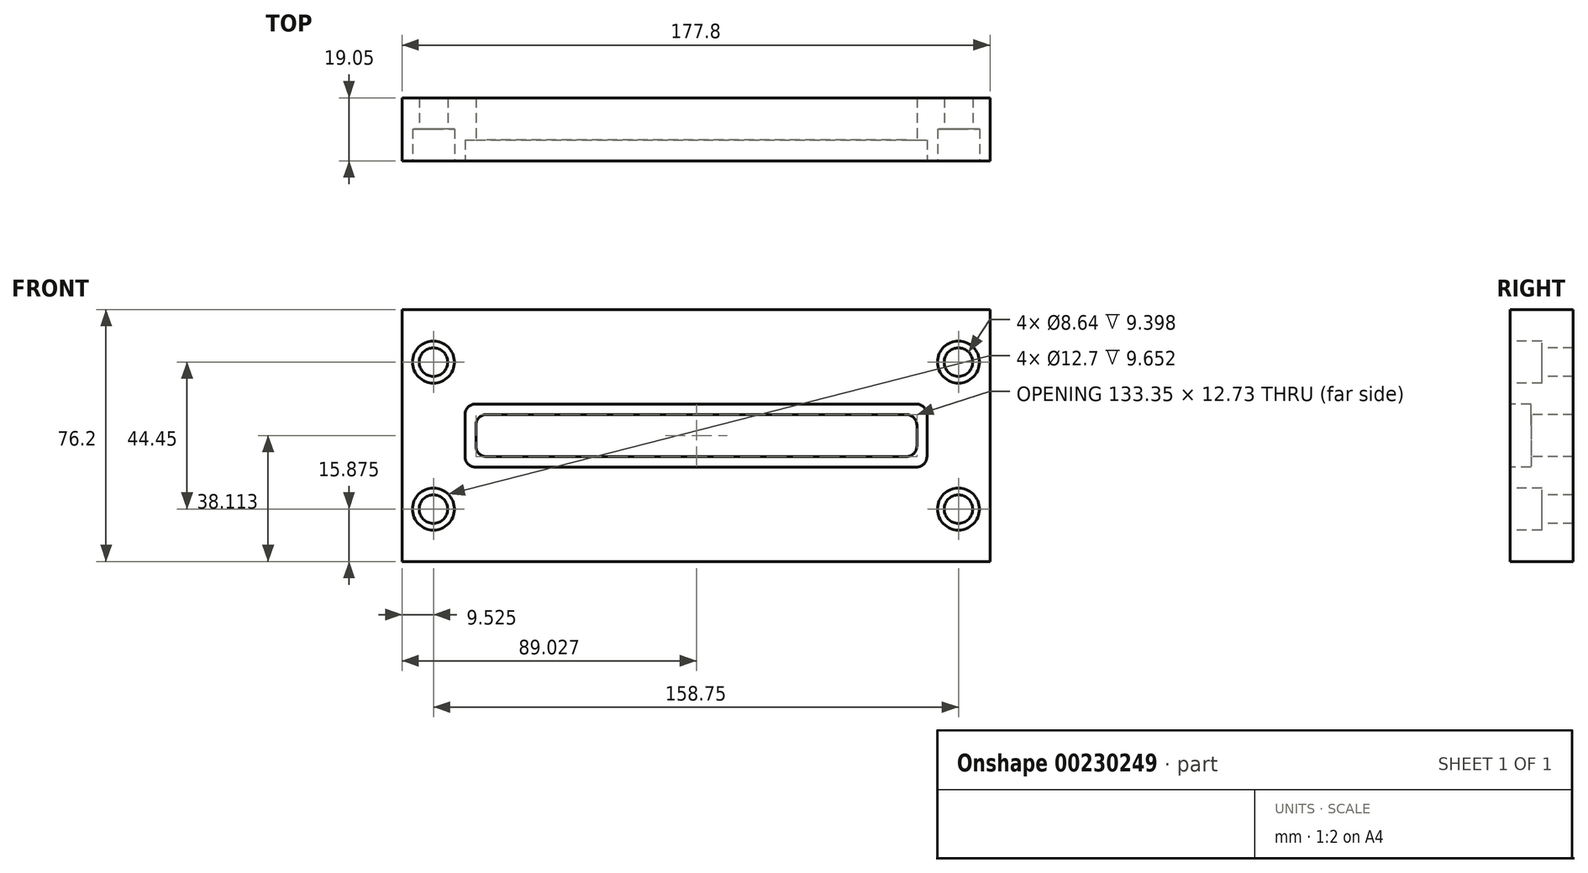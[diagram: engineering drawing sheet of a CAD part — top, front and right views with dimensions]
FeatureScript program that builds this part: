
annotation { "Feature Type Name" : "Feature", "Feature Type Description" : "" }
export const myFeature = defineFeature(function(context is Context, id is Id, definition is map)
    precondition{}
    {
        {
            var Q0;
            Q0=qCreatedBy(makeId("Front.planeOp"),FACE);
            var sketch = newSketch(context, id + "F0", { "sketchPlane" : qUnion([Q0])});
            skLineSegment(sketch, "E0.bottom", {"start": v(0, 0) * mm, "end": v(177.8, 0) * mm});
            skLineSegment(sketch, "E0.top", {"start": v(0, 76.2) * mm, "end": v(177.8, 76.2) * mm});
            skLineSegment(sketch, "E0.left", {"start": v(0, 0) * mm, "end": v(0, 76.2) * mm});
            skLineSegment(sketch, "E0.right", {"start": v(177.8, 0) * mm, "end": v(177.8, 76.2) * mm});
            skSolve(sketch);
        }
        {
            var Q0;
            Q0 = qSketchRegion(id + "F0", true);
            extrude(context, id + "F1", {"entities" : qUnion([Q0]), "depth" : 19.05 * mm});
        }
        {
            var Q0;
            Q0=makeQuery(id+"F1.opExtrude","CAP_FACE",FACE,{"disambiguationData":[OSD([sQuery(id+"F0.wireOp",EDGE,"E0.bottom"),sQuery(id+"F0.wireOp",EDGE,"E0.top"),sQuery(id+"F0.wireOp",EDGE,"E0.left"),sQuery(id+"F0.wireOp",EDGE,"E0.right")])],"isStart":false});
            var sketch = newSketch(context, id + "F2", { "sketchPlane" : qUnion([Q0])});
            skLineSegment(sketch, "E1.bottom", {"start": v(25.53, 31.75) * mm, "end": v(152.53, 31.75) * mm});
            skLineSegment(sketch, "E1.top", {"start": v(25.53, 44.48) * mm, "end": v(152.53, 44.48) * mm});
            skLineSegment(sketch, "E1.left", {"start": v(22.35, 34.92) * mm, "end": v(22.35, 41.3) * mm});
            skLineSegment(sketch, "E1.right", {"start": v(155.7, 34.92) * mm, "end": v(155.7, 41.3) * mm});
            skPoint(sketch, "E2.visualSharp", {"position": v(22.35, 44.48) * mm});
            skArc(sketch, "E2.filletArc", {"start": v(25.53, 44.48) * mm, "mid": v(23.28, 43.55) * mm, "end": v(22.35, 41.3) * mm});
            skPoint(sketch, "E3.visualSharp", {"position": v(22.35, 31.75) * mm});
            skArc(sketch, "E3.filletArc", {"start": v(22.35, 34.92) * mm, "mid": v(23.28, 32.68) * mm, "end": v(25.53, 31.75) * mm});
            skPoint(sketch, "E4.visualSharp", {"position": v(155.7, 31.75) * mm});
            skArc(sketch, "E4.filletArc", {"start": v(152.53, 31.75) * mm, "mid": v(154.77, 32.68) * mm, "end": v(155.7, 34.92) * mm});
            skPoint(sketch, "E5.visualSharp", {"position": v(155.7, 44.48) * mm});
            skArc(sketch, "E5.filletArc", {"start": v(155.7, 41.3) * mm, "mid": v(154.77, 43.55) * mm, "end": v(152.53, 44.48) * mm});
            skSolve(sketch);
        }
        {
            var Q0;
            Q0 = qSketchRegion(id + "F2", true);
            extrude(context, id + "F3", {"entities" : qUnion([Q0]), "operationType" : NewBodyOperationType.REMOVE, "oppositeDirection" : true, "depth" : 25.4 * mm});
        }
        {
            var Q0;
            Q0=makeQuery(id+"F1.opExtrude","CAP_FACE",FACE,{"disambiguationData":[OSD([sQuery(id+"F0.wireOp",EDGE,"E0.bottom"),sQuery(id+"F0.wireOp",EDGE,"E0.top"),sQuery(id+"F0.wireOp",EDGE,"E0.left"),sQuery(id+"F0.wireOp",EDGE,"E0.right")])],"isStart":false});
            var sketch = newSketch(context, id + "F4", { "sketchPlane" : qUnion([Q0])});
            skLineSegment(sketch, "E6.bottom", {"start": v(22.22, 47.65) * mm, "end": v(155.58, 47.65) * mm});
            skLineSegment(sketch, "E6.top", {"start": v(22.22, 28.57) * mm, "end": v(155.58, 28.58) * mm});
            skLineSegment(sketch, "E6.left", {"start": v(19.05, 44.48) * mm, "end": v(19.05, 31.75) * mm});
            skLineSegment(sketch, "E6.right", {"start": v(158.75, 44.48) * mm, "end": v(158.75, 31.75) * mm});
            skPoint(sketch, "E7.visualSharp", {"position": v(19.05, 47.65) * mm});
            skArc(sketch, "E7.filletArc", {"start": v(22.22, 47.65) * mm, "mid": v(19.98, 46.72) * mm, "end": v(19.05, 44.48) * mm});
            skPoint(sketch, "E8.visualSharp", {"position": v(19.05, 28.57) * mm});
            skArc(sketch, "E8.filletArc", {"start": v(19.05, 31.75) * mm, "mid": v(19.98, 29.5) * mm, "end": v(22.22, 28.57) * mm});
            skPoint(sketch, "E9.visualSharp", {"position": v(158.75, 28.58) * mm});
            skArc(sketch, "E9.filletArc", {"start": v(155.58, 28.58) * mm, "mid": v(157.82, 29.5) * mm, "end": v(158.75, 31.75) * mm});
            skPoint(sketch, "E10.visualSharp", {"position": v(158.75, 47.65) * mm});
            skArc(sketch, "E10.filletArc", {"start": v(158.75, 44.48) * mm, "mid": v(157.82, 46.72) * mm, "end": v(155.58, 47.65) * mm});
            skSolve(sketch);
        }
        {
            var Q0;
            Q0 = qSketchRegion(id + "F4", true);
            extrude(context, id + "F5", {"entities" : qUnion([Q0]), "operationType" : NewBodyOperationType.REMOVE, "oppositeDirection" : true, "depth" : 6.35 * mm});
        }
        {
            var Q0;
            Q0=makeQuery(id+"F1.opExtrude","CAP_FACE",FACE,{"disambiguationData":[OSD([sQuery(id+"F0.wireOp",EDGE,"E0.bottom"),sQuery(id+"F0.wireOp",EDGE,"E0.top"),sQuery(id+"F0.wireOp",EDGE,"E0.left"),sQuery(id+"F0.wireOp",EDGE,"E0.right")])],"isStart":false});
            var sketch = newSketch(context, id + "F6", { "sketchPlane" : qUnion([Q0])});
            skLineSegment(sketch, "E11.bottom", {"start": v(9.52, 60.33) * mm, "end": v(168.28, 60.33) * mm});
            skLineSegment(sketch, "E11.top", {"start": v(9.53, 15.87) * mm, "end": v(168.28, 15.88) * mm});
            skLineSegment(sketch, "E11.left", {"start": v(9.52, 60.32) * mm, "end": v(9.53, 15.87) * mm});
            skLineSegment(sketch, "E11.right", {"start": v(168.28, 60.33) * mm, "end": v(168.28, 15.88) * mm});
            skPoint(sketch, "E12", {"position": v(9.52, 60.33) * mm});
            skPoint(sketch, "E13", {"position": v(9.53, 15.87) * mm});
            skPoint(sketch, "E14", {"position": v(168.28, 15.88) * mm});
            skPoint(sketch, "E15", {"position": v(168.28, 60.33) * mm});
            skSolve(sketch);
        }
        {
            var Q0;
            Q0=sQuery(id+"F6.wireOp",VERTEX,"E13");
            var Q1;
            Q1=sQuery(id+"F6.wireOp",VERTEX,"E12");
            var Q2;
            Q2=sQuery(id+"F6.wireOp",VERTEX,"E15");
            var Q3;
            Q3=sQuery(id+"F6.wireOp",VERTEX,"E14");
            var Q4;
            Q4=makeQuery(id+"F1.opExtrude","SWEPT_BODY",BODY,{"disambiguationData":[OSD([sQuery(id+"F0.wireOp",EDGE,"E0.bottom"),sQuery(id+"F0.wireOp",EDGE,"E0.top"),sQuery(id+"F0.wireOp",EDGE,"E0.left"),sQuery(id+"F0.wireOp",EDGE,"E0.right")])]});
            hole(context, id + "F7", {"style" : HoleStyle.C_BORE, "endStyle" : HoleEndStyle.THROUGH, "holeDiameter" : 8.64 * mm, "cBoreDiameter" : 12.7 * mm, "cBoreDepth" : 9.65 * mm, "locations" : qUnion([Q0, Q1, Q2, Q3]), "scope" : qUnion([Q4]), "isTappedThrough" : true});
        }
    });
